# Revit family: IS_CerathermT125_A7589_BIM_FR
name_source: partatom
category: Plumbing Fixtures
units: mm (PartAtom-declared; Revit-internal decimal feet)

## family parameters
Always vertical = No
Cut with Voids When Loaded = No
OmniClass Number = 23.45.55.17
OmniClass Title = Mixing Faucets
Part Type = Normal
Room Calculation Point = No
Round Connector Dimension = Use Diameter
Shared = No
Work Plane-Based = No

## types (4) — shared parameters
Accessories = https://www.idealstandard.fr
AreaUnits = millimeters
AssetType = Plumbing Fittures
Auteur = Ideal Standard
BIMObjectName = IS_IdealStandard_Showermixers_Ceratherm T125  _A7589
BIMobject category = Taps & Mixers
BIMobject category code = sanitary-taps-mixers
BIMobject main category = Sanitary
BIMobject main category code = sanitary
Bim-NomDuProjet = IS_IdealStandard_Showermixers_Ceratherm T125  _A7589
Brand = Ideal Standard
Brand url = http://www.idealstandard.fr
Category = Plumbing Fixtures
Classification = Shower Mixers
ConnectionType = Plumbing
ConseilsDInstallation = https://www.idealstandard.fr
CurrencyUnit = €
CurrentRevision = 1
Date of publishing = 14/04/2022
DateDeCréation = 14/04/2022
Dimensions = 358 x 577 x 1348 mm
DurationUnit = Years
DuréeDeGarantieDesPièces = 5
DuréeGarantie = 5
DétailGarantie = https://www.idealstandard.fr
Edition number = 1
EffectuéPar = 1
Espace = Interne
FaucetFunction = Manual Shower Mixer
FaucetOperation = Manual Shower Mixers
FaucetTopDescription = Manual Shower Mixer
Forme = Cylindrique
GTIN code = https://4015413351737
Help = https://www.idealstandard.fr
IFC Classification = Sanitary Terminal
IfcExportAs = IfcValveType
IfcExportType = FAUCET
InformationsProduit = https://www.idealstandard.fr
Installation instructions = https://www.idealstandard.fr
InstallationInstructions = https://www.idealstandard.fr
Largeur = 358 mm
LinearUnits = millimeters
Longueur = 577 mm
MaintenanceInformation = https://www.idealstandard.fr
Manufacturer = Ideal Standard
Manufacturer name = Ideal Standard
ManufacturerURL = https://www.idealstandard.fr
Marque = Ideal Standard
Material = Brass
Material main = Brass
Matériel = laiton
NBS Reference Code = 45-35-70/335
NBS Reference Description = Shower mixers
Name = Showermixers_Ceratherm T125 _A7589_IdealStandard
NettWeight = 4.4
Nom = Showermixers_Ceratherm T125 _A7589_IdealStandard
NominalDepth = 577 mm
NominalHeight = 1348 mm
NominalLength = 577 mm
NominalWidth = 358 mm
PiècesDétachées = https://www.idealstandard.fr
PoidsNet = 4.4
PoignéesDePréhension = No
Product Guid = b52b51ea-52fb-4d6a-816c-d6271685112e
Product SKU = A7589
Product certification = https://www.idealstandard.fr
Product data url = https://bimobject.com
Product family = CERATHERM
Product group = Taps & Mixers
Product url = https://www.idealstandard.fr
ProductInformation = https://www.idealstandard.fr
Profondeur = 577 mm
QR code = http://bimobject.com
Receveur = No
Révision = 1
Shape = cylindrical
ShowerType = Shower Mixer
Size = 358 x 577 x 1348 mm
Space = internal
SpareParts = https://www.idealstandard.fr
Technical description = https://www.idealstandard.fr
TechnologieDeLaRobinetterie = mitigeur thermostatique pour robinet de douche
TestDePression = 10
TestPressure = 10 bar
TypeDeRobinetterie = mitigeur thermostatique pour robinet de douche
UNSPSC Code = 301815
URL = https://www.idealstandard.fr
Uniclass 1.4 Code = L725111
Uniclass 1.4 Description = Mixer Taps
Uniclass 2.0 Code = PR-35-06-82
Uniclass 2.0 Description = Shower Mixers
Uniclass 2015 Code = Pr_40_20_87_78
Uniclass 2015 Name = Shower manual water supply sets
Uniclass2015Code = Pr_40_20_87_78
Uniclass2015Title = Shower manual water supply sets
Uniclass2015Version = v1.25
Uniformat II Code = C1030
Uniformat II Description = Fittings
UnitéDeMesure = millimètres
UnitéDeTemps = ans
UnitéMonétaire = Euro
UrlDuFabricant = https://www.idealstandard.fr
UsageDeLaRobinetterie = mitigeur thermostatique pour robinet de douche
Version = 1
VolumeUnits = Litres
WRASURL = https://www.wrasapprovals.co.uk
WarrantyDescription = Manufacturer warranty
WarrantyDurationParts = 5
WarrantyDurationUnit = years
Youtube clip = https://www.youtube.com
zero-valued in all types: CoûtDeRemplacement, Hauteur, MaterialThickness, PressionDeFonctionnement

## per-type parameters (varying)
| type | BarCode | Caractéristiques | CodeBarre | Color | Couleur | Description | DescriptionDeLaRobinetterie | Features | Finish | Finition | MainColor | Model | ModelNumber | ModelReference | Product name | Référence |
| A7589GN - CERATHERM T125 EXPOSED SHOWER SYSTEM MIXER - SILVER STORM | 4015413352543 | Système de douche à inverseur thermostatique avec colonne montante fixe, douche à effet pluie en métal de 300 mm, douchette à main et connecteur en S - Silver Storm | 4015413352543 | Silver Storm | Argent | Ceratherm T125 thermostatic diverter shower system with fixed riser, 300mm metal rain shower, stick hand shower and S-Connector - Silver Storm | Système de douche à inverseur thermostatique Ceratherm T125 avec colonne montante fixe, douche à effet pluie en métal de 300 mm, douchette à main et connecteur en S - Silver Storm | Thermostatic diverter shower system with fixed riser, 300mm metal rain shower, stick hand shower and S-Connector - Silver Storm | Silver Storm | Tempête d'argent | Silver Storm | A7589GN | A7589GN | CERATHERM T125 EXPOSED SHOWER SYSTEM MIXER - SILVER STORM | CERATHERM T125 EXPOSED SHOWER SYSTEM MIXER | CERATHERM T125 EXPOSED SHOWER SYSTEM MIXER - SILVER STORM |
| A7589AA - CERATHERM T125 EXPOSED SHOWER SYSTEM MIXER - CHROME | 4015413351737 | Système de douche à inverseur thermostatique avec colonne montante fixe, douche à effet pluie en métal de 300 mm, douchette à main et connecteur en S - Chrome | 4015413351737 | Chrome | Chrome | Ceratherm T125 thermostatic diverter shower system with fixed riser, 300mm metal rain shower, stick hand shower and S-Connector - Chrome | Système de douche à inverseur thermostatique Ceratherm T125 avec colonne montante fixe, douche à effet pluie en métal de 300 mm, douchette à main et connecteur en S - Chrome | Thermostatic diverter shower system with fixed riser, 300mm metal rain shower, stick hand shower and S-Connector - Chrome | Chrome | Chrome | Chrome | A7589AA | A7589AA | CERATHERM T125 EXPOSED SHOWER SYSTEM MIXER - CHROME | CERATHERM T 125 EXPOSED SHOWER SYSTEM MIXER | CERATHERM T125 EXPOSED SHOWER SYSTEM MIXER - CHROME |
| A7589A5 - CERATHERM T125 EXPOSED SHOWER SYSTEM MIXER - MAGNETIC GREY | 4015413352536 | Système de douche à inverseur thermostatique avec colonne montante fixe, douche à effet pluie en métal de 300 mm, douchette à main et connecteur en S - Gris magnétique | 4015413352536 | Magnetic Grey | gris margenique | Ceratherm T125 thermostatic diverter shower system with fixed riser, 300mm metal rain shower, stick hand shower and S-Connector - Magnetic Grey | Système de douche à inverseur thermostatique Ceratherm T125 avec colonne montante fixe, douche à effet pluie en métal de 300 mm, douchette à main et connecteur en S - Gris magnétique | Thermostatic diverter shower system with fixed riser, 300mm metal rain shower, stick hand shower and S-Connector - Magnetic Grey | Magnetic Grey | Gris magnétique | Magnetic Grey | A7589A5 | A7589A5 | CERATHERM T125 EXPOSED SHOWER SYSTEM MIXER - MAGNETIC GREY | CERATHERM T125 EXPOSED SHOWER SYSTEM MIXER | CERATHERM T125 EXPOSED SHOWER SYSTEM MIXER - MAGNETIC GREY |
| A7589A2 - CERATHERM T125 EXPOSED SHOWER SYSTEM MIXER - BRUSH GOLD | 4015413352529 | Système de douche à inverseur thermostatique avec colonne montante fixe, douche à effet pluie en métal de 300 mm, douchette à main et connecteur en S - Brush Gold | 4015413352529 | Brush Gold | Or | Ceratherm T125 thermostatic diverter shower system with fixed riser, 300mm metal rain shower, stick hand shower and S-Connector - Brush Gold | Système de douche à inverseur thermostatique Ceratherm T125 avec colonne montante fixe, douche à effet pluie en métal de 300 mm, douchette à main et connecteur en S - Brush Gold | Thermostatic diverter shower system with fixed riser, 300mm metal rain shower, stick hand shower and S-Connector - Brush Gold | Brush Gold | Pinceau Or | Brush Gold | A7589A2 | A7589A2 | CERATHERM T125 EXPOSED SHOWER SYSTEM MIXER - BRUSH GOLD | CERATHERM T125 EXPOSED SHOWER SYSTEM MIXER | CERATHERM T125 EXPOSED SHOWER SYSTEM MIXER - BRUSH GOLD |

## geometry (parser evidence)
native form markers: Sweep x4
no freeform markers — native parametric forms only
